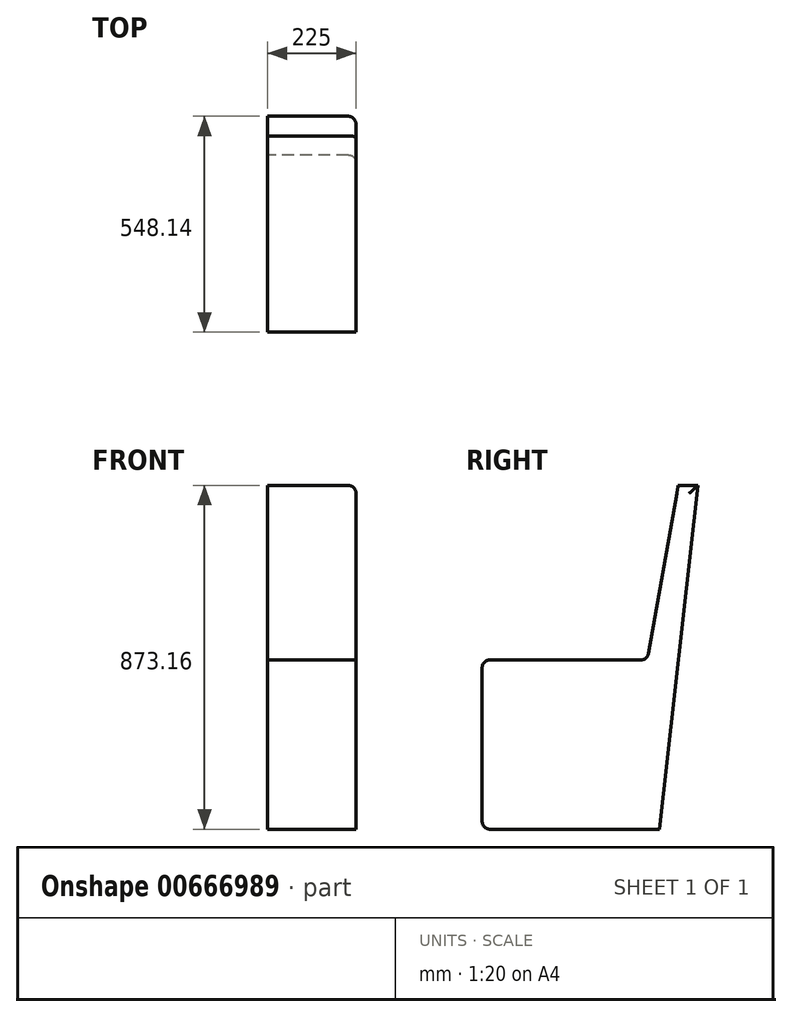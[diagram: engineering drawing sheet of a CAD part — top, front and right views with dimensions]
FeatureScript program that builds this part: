
annotation { "Feature Type Name" : "Feature", "Feature Type Description" : "" }
export const myFeature = defineFeature(function(context is Context, id is Id, definition is map)
    precondition{}
    {
        {
            var Q0;
            Q0=qCreatedBy(makeId("Right.planeOp"),FACE);
            var sketch = newSketch(context, id + "F0", { "sketchPlane" : qUnion([Q0])});
            skLineSegment(sketch, "E0", {"start": v(0, 0) * mm, "end": v(-450, 0) * mm});
            skLineSegment(sketch, "E1", {"start": v(-450, 0) * mm, "end": v(-450, 430) * mm});
            skLineSegment(sketch, "E2", {"start": v(-450, 430) * mm, "end": v(-30, 430) * mm});
            skLineSegment(sketch, "E3", {"start": v(-30, 430) * mm, "end": v(48.14, 873.16) * mm});
            skLineSegment(sketch, "E4", {"start": v(48.14, 873.16) * mm, "end": v(98.14, 873.16) * mm});
            skLineSegment(sketch, "E5", {"start": v(98.14, 873.16) * mm, "end": v(0, 0) * mm});
            skSolve(sketch);
        }
        {
            var Q0;
            Q0=makeQuery(id+"F0.imprint","IMPRINT",FACE,{"disambiguationData":[TD([[makeQuery(id+"F0.imprint","IMPRINT",EDGE,{"derivedFrom":sQuery(id+"F0.wireOp",EDGE,"E0")}),-1.0]])]});
            extrude(context, id + "F1", {"entities" : qUnion([Q0]), "depth" : 225 * mm, "offsetDistance" : 25 * mm});
        }
        {
            var Q0;
            Q0=makeQuery(id+"F1.opExtrude","CAP_EDGE",EDGE,{"disambiguationData":[OSD([sQuery(id+"F0.wireOp",EDGE,"E4")])],"isStart":false});
            var Q1;
            Q1=makeQuery(id+"F1.opExtrude","CAP_EDGE",EDGE,{"disambiguationData":[OSD([sQuery(id+"F0.wireOp",EDGE,"E5")])],"isStart":false});
            var Q2;
            Q2=makeQuery(id+"F1.opExtrude","SWEPT_EDGE",EDGE,{"disambiguationData":[OSD([sQuery(id+"F0.wireOp",EDGE,"E2"),sQuery(id+"F0.wireOp",EDGE,"E3")])]});
            var Q3;
            Q3=makeQuery(id+"F1.opExtrude","SWEPT_EDGE",EDGE,{"disambiguationData":[OSD([sQuery(id+"F0.wireOp",EDGE,"E1"),sQuery(id+"F0.wireOp",EDGE,"E2")])]});
            var Q4;
            Q4=makeQuery(id+"F1.opExtrude","SWEPT_EDGE",EDGE,{"disambiguationData":[OSD([sQuery(id+"F0.wireOp",EDGE,"E0"),sQuery(id+"F0.wireOp",EDGE,"E1")])]});
            fillet(context, id + "F2", {"entities" : qUnion([Q0, Q1, Q2, Q3, Q4]), "radius" : 20 * mm, "tangentPropagation" : true, "allowEdgeOverflow" : false});
        }
    });
